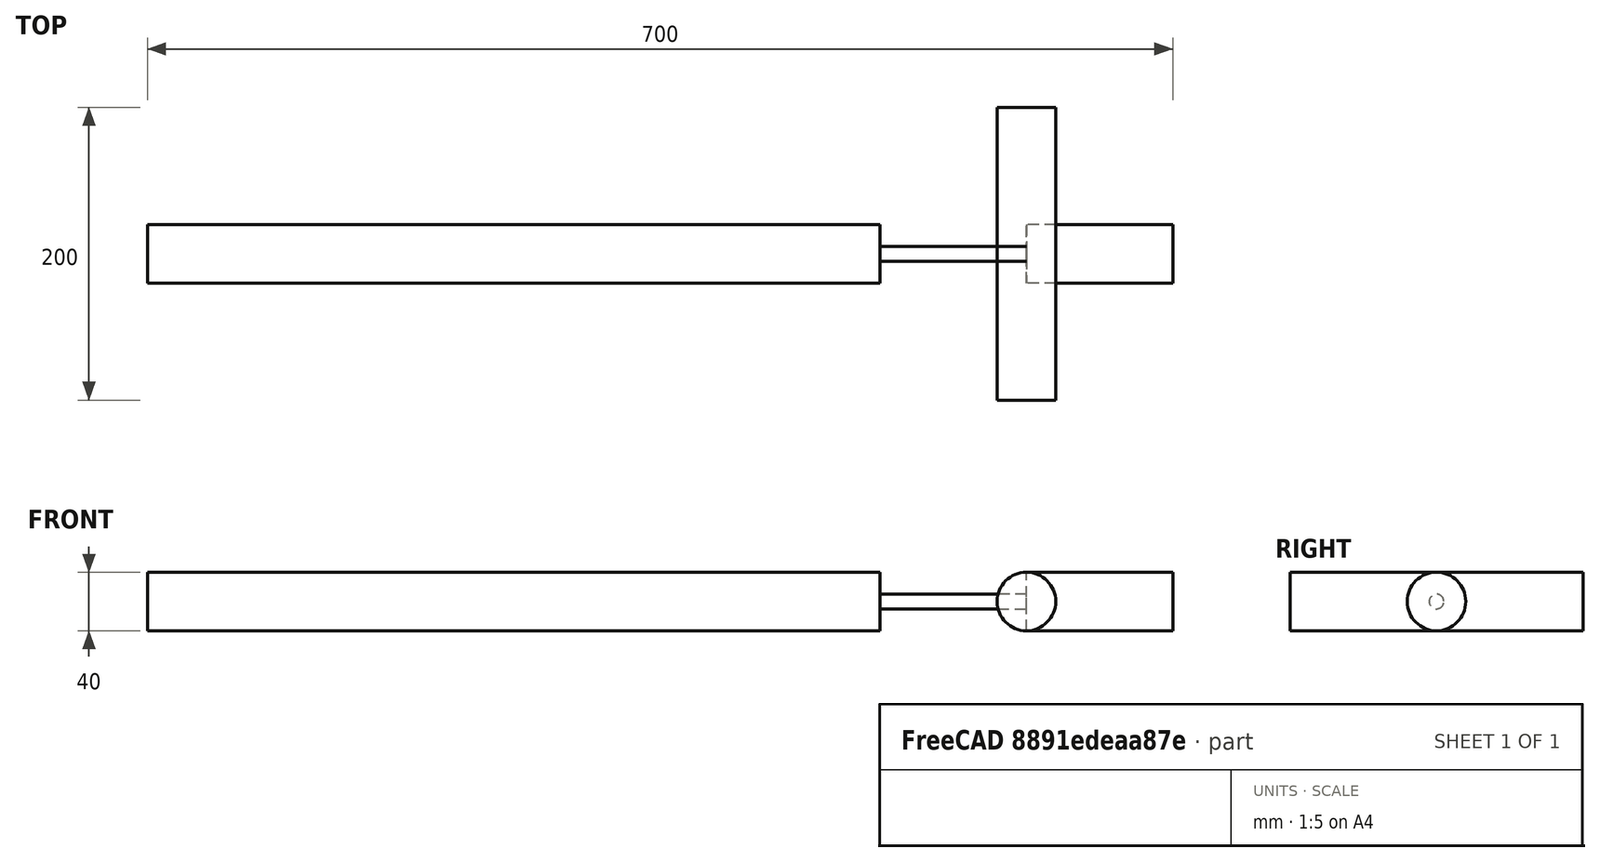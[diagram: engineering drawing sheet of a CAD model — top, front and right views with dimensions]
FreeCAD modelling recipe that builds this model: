
FCSTD DOCUMENT  (FreeCAD 0.20R29177 (Git))
Label: model
License: All rights reserved
LicenseURL: http://en.wikipedia.org/wiki/All_rights_reserved
objects: Part::Feature×9, Part::Cylinder×4
note: 13 computed .brp shape members not serialized (recipe doc carries the construction recipe); baked Part::Feature solids carry a one-line shape summary decoded from their .brp

FEATURE [Part::Cylinder] Cylinder  label="円柱"
  Angle = 360
  AttacherType = Attacher::AttachEngine3D
  FirstAngle = 0
  Height = 100
  Placement = pos=(500,0,0) rot=(0,1,0;1.5708rad)
  Radius = 5
  SecondAngle = 0
FEATURE [Part::Cylinder] Cylinder001  label="円柱001"
  Angle = 360
  AttacherType = Attacher::AttachEngine3D
  FirstAngle = 0
  Height = 200
  Placement = pos=(600,100,0) rot=(1,0,0;1.5708rad)
  Radius = 20
  SecondAngle = 0
FEATURE [Part::Cylinder] Cylinder002  label="円柱002"
  Angle = 360
  AttacherType = Attacher::AttachEngine3D
  FirstAngle = 0
  Height = 500
  Placement = pos=(0,0,0) rot=(0,1,0;1.5708rad)
  Radius = 20
  SecondAngle = 0
FEATURE [Part::Cylinder] Cylinder003  label="円柱003"
  Angle = 360
  AttacherType = Attacher::AttachEngine3D
  FirstAngle = 0
  Height = 100
  Placement = pos=(600,0,0) rot=(0,1,0;1.5708rad)
  Radius = 20
  SecondAngle = 0
FEATURE [Part::Feature] Face  label="sideWall3"
  shape: bbox 100 x 40 x 40 mm, 1 faces, 0 solids (baked)
FEATURE [Part::Feature] Face001  label="wallOutlet1"
  shape: bbox 40 x 200 x 40 mm, 1 faces, 0 solids (baked)
FEATURE [Part::Feature] Face002  label="outletXmax"
  Placement = pos=(700,0,-2.22e-14) rot=(0,1,0;1.5708rad)
  shape: bbox 2e-07 x 40 x 40 mm, 1 faces, 0 solids (baked)
FEATURE [Part::Feature] Face003  label="outletYmax"
  Placement = pos=(600,100,0) rot=(1,0,0;1.5708rad)
  shape: bbox 40 x 2e-07 x 40 mm, 1 faces, 0 solids (baked)
FEATURE [Part::Feature] Face004  label="outletYmin"
  Placement = pos=(600,-100,-4.44e-14) rot=(1,0,0;1.5708rad)
  shape: bbox 40 x 2e-07 x 40 mm, 1 faces, 0 solids (baked)
FEATURE [Part::Feature] Face005  label="sideWall2"
  shape: bbox 80.64 x 10 x 10 mm, 1 faces, 0 solids (baked)
FEATURE [Part::Feature] Face006  label="wall1"
  shape: bbox 2e-07 x 40 x 40 mm, 1 faces, 0 solids (baked)
FEATURE [Part::Feature] Face007  label="sideWall1"
  Placement = pos=(0,0,0) rot=(0,1,0;1.5708rad)
  shape: bbox 500 x 40 x 40 mm, 1 faces, 0 solids (baked)
FEATURE [Part::Feature] Face008  label="inlet"
  Placement = pos=(0,0,0) rot=(0,1,0;1.5708rad)
  shape: bbox 2e-07 x 40 x 40 mm, 1 faces, 0 solids (baked)
